# Revit family: Hager-Univers-IP55-D275-H1550-Cl.II-Steel_encl-CH-it
name_source: partatom
category: Equipement électrique
units: mm (PartAtom-declared; Revit-internal decimal feet)

## family parameters
Configuration du panneau = Deux colonnes, circuits au sein
Cote de connecteur circulaire = Utiliser le diamètre
Couper avec des vides une fois chargée = Non
Hôte = Face
Partagée = Non
Point de calcul de pièce = Non
Type d'élément = Tableau de raccordement

## types (5) — shared parameters
Commentaires du type = Univers
EF000003 - Tipo di montaggio = EV000384 - A parete
EF000007 - colore = EV000270 - grigio
EF000040 - Altezza = 1550 mm  [stored 5.0853 ft]
EF000049 - profondità = 275 mm
EF000116 - numero RAL = 7035
EF000118 - con piastra di montaggio = Non
EF000266 - numero di file = 10
EF000339 - tipo di copertura = EV004216 - porta
EF001088 - possibilità di applicazione = Oui
EF001131 - profondità interna = 275 mm
EF001596 - Attacco Lampada = EV000179 - acciaio
EF001613 - Integrità del circuito = EV000494 - senza
EF002950 - Numero moduli DIN = 24
EF003532 - adatto per uso esterno = Non
EF004293 - resistenza agli urti = EV008784 - IK10
EF005474 - grado di protezione (IP) = EV006420 - IP55
EF006244 - coperchio/porta trasparente = Non
EF006306 - con serratura = Non
EF007800 - adatto per parafulmine = Non
EF008873 - corrente nominale (In) = 800 A
EF009170 - spessore materiale scatola = 2 mm  [stored 0.00656168 ft]
EF009171 - spessore materiale porta/coperchio = 2 mm  [stored 0.00656168 ft]
EF009212 - esecuzione coperchio = EV000116 - chiuso
EF015940 - Coprire con rilascio di sovrapressione = Non
Fabricant = Hager
HG000002 - Con porta = Oui
HG000003 - Gamma = Univers
HG000006 - Ad incasso = Non
HG000023 - Custodia a doppia sezione = Non
HG000024 - Altezza della sezione inferiore = 800 mm  [stored 2.62467 ft]
HG000026 - A pavimento = Non
zero-valued in all types: EF000218 - profondità di incasso, Elévation par défaut, HG000027 - Altezza dello zoccolo

## per-type parameters (varying)
| type | EF000008 - Larghezza | EF000437 - numero di ingressi per conduttori | EF004427 - numero di moduli | EF004464 - tipo di porta | EF009554 - numero delle aperture per la piastra della flangia | HG000004 - Codice produttore | HG000009 - Porta doppia a battente | HG000010 - Porte asimmetriche |
| A parete IP55 L1050 A1550 P275  - FR04S | 1050 mm | 8 | 480 | EV003602 - doppio | 8 | FR04S | Oui | Non |
| A parete IP55 L1300 A1550 P275  - FR05S | 1300 mm  [stored 4.26509 ft] | 10 | 600 | EV003602 - doppio | 10 | FR05S | Oui | Oui |
| A parete IP55 L300 A1550 P275  - FR01S | 300 mm | 2 | 120 | EV002646 - singolo | 2 | FR01S | Non | Non |
| A parete IP55 L550 A1550 P275  - FR02S | 550 mm | 4 | 240 | EV002646 - singolo | 4 | FR02S | Non | Non |
| A parete IP55 L800 A1550 P275  - FR03S | 800 mm  [stored 2.62467 ft] | 6 | 360 | EV002646 - singolo | 6 | FR03S | Non | Non |

note: [stored X ft] marks values corroborated as IEEE doubles in the binary element streams (Revit-internal decimal feet)

## geometry (parser evidence)
native form markers: Sweep x10
no freeform markers — native parametric forms only
